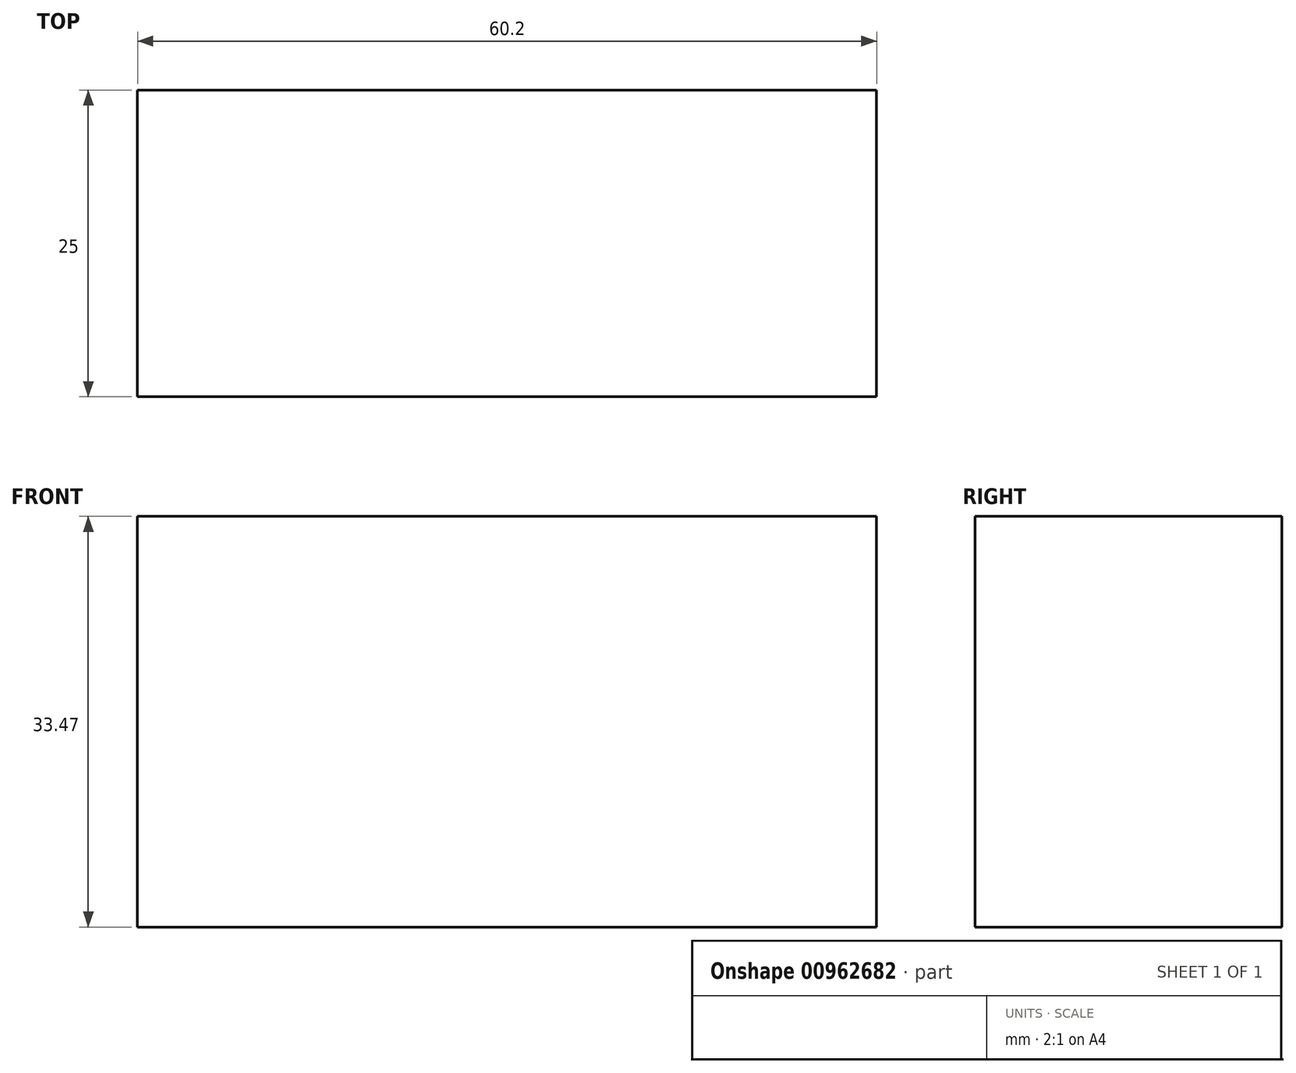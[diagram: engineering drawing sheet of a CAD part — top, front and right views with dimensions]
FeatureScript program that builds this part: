
annotation { "Feature Type Name" : "Feature", "Feature Type Description" : "" }
export const myFeature = defineFeature(function(context is Context, id is Id, definition is map)
    precondition{}
    {
        {
            var Q0;
            Q0=qCreatedBy(makeId("Front.planeOp"),FACE);
            var sketch = newSketch(context, id + "F0", { "sketchPlane" : qUnion([Q0])});
            skLineSegment(sketch, "E0.bottom", {"start": v(-57.42, 50.2) * mm, "end": v(2.78, 50.2) * mm});
            skLineSegment(sketch, "E0.top", {"start": v(-57.42, 16.73) * mm, "end": v(2.78, 16.73) * mm});
            skLineSegment(sketch, "E0.left", {"start": v(-57.42, 50.2) * mm, "end": v(-57.42, 16.73) * mm});
            skLineSegment(sketch, "E0.right", {"start": v(2.78, 50.2) * mm, "end": v(2.78, 16.73) * mm});
            skSolve(sketch);
        }
        {
            var Q0;
            Q0 = qSketchRegion(id + "F0", true);
            extrude(context, id + "F1", {"entities" : qUnion([Q0]), "depth" : 25 * mm, "offsetDistance" : 25 * mm});
        }
    });
